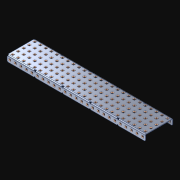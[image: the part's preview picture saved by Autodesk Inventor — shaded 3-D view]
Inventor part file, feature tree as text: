
AUTODESK INVENTOR PART (.ipt)
format: ipt  version: 2021 (Build 250183000, 183)  size: 2,157,568 bytes
history: native  units: in
note: dims shown in document units (in); Inventor stores cm internally (conversion verified against a paired STEP export)
features: extrude x176, other x176, sketch x4, pattern_linear x3
ambient origin geometry x8: Origin, YZ Plane, XZ Plane, XY Plane, X Axis, Y Axis, Z Axis, Center Point
bodies: Solid1 (feature_tree)
feature tree (359):
  pattern_linear  "Rectangular Pattern1"  Spacing1=0.182in  [1 undecoded]
  pattern_linear  "Rectangular Pattern2"  Spacing1=0.046in  [1 undecoded]
  pattern_linear  "Rectangular Pattern3"  Spacing1=0.5in  [1 undecoded]
  extrude  "Extrusion1"  Depth=9.8425in
  sketch  "Sketch1"  dims[d0=0.182in]
  other  "Srf1"
  sketch  "Sketch2"  dims[d1=0.046in d2=0.0in]
  other  "Srf2"
  sketch  "Sketch3"  dims[d3=0.182in]
  other  "Srf3"
  other  "Srf4"
  other  "Srf5"
  other  "Srf6"
  other  "Srf7"
  other  "Srf8"
  other  "Srf9"
  other  "Srf10"
  other  "Srf11"
  other  "Srf12"
  other  "Srf13"
  other  "Srf14"
  other  "Srf15"
  other  "Srf16"
  other  "Srf17"
  other  "Srf18"
  other  "Srf19"
  other  "Srf20"
  other  "Srf21"
  other  "Srf22"
  other  "Srf23"
  other  "Srf24"
  other  "Srf25"
  other  "Srf26"
  other  "Srf27"
  other  "Srf38"
  other  "Srf39"
  other  "Srf40"
  other  "Srf41"
  other  "Srf42"
  other  "Srf43"
  other  "Srf44"
  other  "Srf45"
  other  "Srf46"
  other  "Srf47"
  other  "Srf48"
  other  "Srf49"
  other  "Srf50"
  other  "Srf51"
  other  "Srf52"
  other  "Srf53"
  other  "Srf54"
  other  "Srf55"
  other  "Srf56"
  other  "Srf57"
  other  "Srf58"
  other  "Srf59"
  other  "Srf60"
  other  "Srf61"
  other  "Srf72"
  other  "Srf73"
  other  "Srf74"
  other  "Srf75"
  other  "Srf76"
  other  "Srf77"
  other  "Srf78"
  other  "Srf79"
  other  "Srf80"
  other  "Srf81"
  other  "Srf82"
  other  "Srf83"
  other  "Srf84"
  other  "Srf85"
  other  "Srf86"
  other  "Srf87"
  other  "Srf88"
  other  "Srf89"
  other  "Srf90"
  other  "Srf91"
  other  "Srf92"
  other  "Srf93"
  other  "Srf94"
  other  "Srf95"
  other  "Srf96"
  other  "Srf107"
  other  "Srf108"
  other  "Srf109"
  other  "Srf110"
  other  "Srf111"
  other  "Srf112"
  other  "Srf113"
  other  "Srf114"
  other  "Srf115"
  other  "Srf116"
  other  "Srf117"
  other  "Srf118"
  other  "Srf119"
  other  "Srf120"
  other  "Srf121"
  other  "Srf122"
  other  "Srf123"
  other  "Srf124"
  other  "Srf125"
  other  "Srf126"
  other  "Srf127"
  other  "Srf128"
  other  "Srf129"
  other  "Srf130"
  other  "Srf131"
  other  "Srf142"
  other  "Srf143"
  other  "Srf144"
  other  "Srf145"
  other  "Srf146"
  other  "Srf147"
  other  "Srf148"
  other  "Srf149"
  other  "Srf150"
  other  "Srf151"
  other  "Srf152"
  other  "Srf153"
  other  "Srf154"
  other  "Srf155"
  other  "Srf156"
  other  "Srf157"
  other  "Srf158"
  other  "Srf159"
  other  "Srf160"
  other  "Srf161"
  other  "Srf162"
  other  "Srf163"
  other  "Srf164"
  other  "Srf165"
  other  "Srf166"
  other  "Srf177"
  other  "Srf178"
  other  "Srf179"
  other  "Srf180"
  other  "Srf181"
  other  "Srf182"
  other  "Srf183"
  other  "Srf184"
  other  "Srf185"
  other  "Srf186"
  other  "Srf187"
  other  "Srf188"
  other  "Srf189"
  other  "Srf190"
  other  "Srf191"
  other  "Srf192"
  other  "Srf193"
  other  "Srf194"
  other  "Srf195"
  other  "Srf196"
  other  "Srf197"
  other  "Srf198"
  other  "Srf199"
  other  "Srf200"
  other  "Srf201"
  other  "Srf212"
  other  "Srf213"
  other  "Srf214"
  other  "Srf215"
  other  "Srf216"
  other  "Srf217"
  other  "Srf218"
  other  "Srf219"
  other  "Srf220"
  other  "Srf221"
  other  "Srf222"
  other  "Srf223"
  other  "Srf224"
  other  "Srf225"
  other  "Srf226"
  other  "Srf227"
  other  "Srf228"
  other  "Srf229"
  other  "Srf230"
  other  "Srf231"
  other  "Srf232"
  other  "Srf233"
  other  "Srf234"
  other  "Srf235"
  sketch  "Sketch4"  dims[d4=0.046in d5=0.0in d6=0.182in d7=0.046in d8=0.0in d11=0.5in d12=9.8425in d14=0.5in d15=1.9685in d17=0.5in d18=9.8425in d20=0.5in d21=5.0in d22=0.0in]
  parser-record x1  (decoder bookkeeping rows leaked as tree rows — omitted from the tree; the rows remain in map.json)
  extrude  "ExtrusionSrf1"  Depth=9.8425in
  extrude  "ExtrusionSrf2"  Depth=9.8425in
  extrude  "ExtrusionSrf3"  Depth=9.8425in
  extrude  "ExtrusionSrf4"  Depth=9.8425in
  extrude  "ExtrusionSrf5"  Depth=9.8425in
  extrude  "ExtrusionSrf6"  TaperAngle=0.0deg  [1 undecoded]
  extrude  "ExtrusionSrf7"  [1 undecoded]
  extrude  "ExtrusionSrf8"  [1 undecoded]
  extrude  "ExtrusionSrf9"  [1 undecoded]
  extrude  "ExtrusionSrf10"  [1 undecoded]
  extrude  "ExtrusionSrf11"  [1 undecoded]
  extrude  "ExtrusionSrf12"  [1 undecoded]
  extrude  "ExtrusionSrf13"  [1 undecoded]
  extrude  "ExtrusionSrf14"  [1 undecoded]
  extrude  "ExtrusionSrf15"  [1 undecoded]
  extrude  "ExtrusionSrf16"  [1 undecoded]
  extrude  "ExtrusionSrf17"  [1 undecoded]
  extrude  "ExtrusionSrf18"  [1 undecoded]
  extrude  "ExtrusionSrf19"  [1 undecoded]
  extrude  "ExtrusionSrf20"  [1 undecoded]
  extrude  "ExtrusionSrf21"  [1 undecoded]
  extrude  "ExtrusionSrf22"  [1 undecoded]
  extrude  "ExtrusionSrf23"  [1 undecoded]
  extrude  "ExtrusionSrf24"  [1 undecoded]
  extrude  "ExtrusionSrf25"  [1 undecoded]
  extrude  "ExtrusionSrf26"  [1 undecoded]
  extrude  "ExtrusionSrf27"  [1 undecoded]
  extrude  "ExtrusionSrf38"  [1 undecoded]
  extrude  "ExtrusionSrf39"  [1 undecoded]
  extrude  "ExtrusionSrf40"  [1 undecoded]
  extrude  "ExtrusionSrf41"  [1 undecoded]
  extrude  "ExtrusionSrf42"  [1 undecoded]
  extrude  "ExtrusionSrf43"  [1 undecoded]
  extrude  "ExtrusionSrf44"  [1 undecoded]
  extrude  "ExtrusionSrf45"  [1 undecoded]
  extrude  "ExtrusionSrf46"  [1 undecoded]
  extrude  "ExtrusionSrf47"  [1 undecoded]
  extrude  "ExtrusionSrf48"  [1 undecoded]
  extrude  "ExtrusionSrf49"  [1 undecoded]
  extrude  "ExtrusionSrf50"  [1 undecoded]
  extrude  "ExtrusionSrf51"  [1 undecoded]
  extrude  "ExtrusionSrf52"  [1 undecoded]
  extrude  "ExtrusionSrf53"  [1 undecoded]
  extrude  "ExtrusionSrf54"  [1 undecoded]
  extrude  "ExtrusionSrf55"  [1 undecoded]
  extrude  "ExtrusionSrf56"  [1 undecoded]
  extrude  "ExtrusionSrf57"  [1 undecoded]
  extrude  "ExtrusionSrf58"  [1 undecoded]
  extrude  "ExtrusionSrf59"  [1 undecoded]
  extrude  "ExtrusionSrf60"  [1 undecoded]
  extrude  "ExtrusionSrf61"  [1 undecoded]
  extrude  "ExtrusionSrf72"  [1 undecoded]
  extrude  "ExtrusionSrf73"  [1 undecoded]
  extrude  "ExtrusionSrf74"  [1 undecoded]
  extrude  "ExtrusionSrf75"  [1 undecoded]
  extrude  "ExtrusionSrf76"  [1 undecoded]
  extrude  "ExtrusionSrf77"  [1 undecoded]
  extrude  "ExtrusionSrf78"  [1 undecoded]
  extrude  "ExtrusionSrf79"  [1 undecoded]
  extrude  "ExtrusionSrf80"  [1 undecoded]
  extrude  "ExtrusionSrf81"  [1 undecoded]
  extrude  "ExtrusionSrf82"  [1 undecoded]
  extrude  "ExtrusionSrf83"  [1 undecoded]
  extrude  "ExtrusionSrf84"  [1 undecoded]
  extrude  "ExtrusionSrf85"  [1 undecoded]
  extrude  "ExtrusionSrf86"  [1 undecoded]
  extrude  "ExtrusionSrf87"  [1 undecoded]
  extrude  "ExtrusionSrf88"  [1 undecoded]
  extrude  "ExtrusionSrf89"  [1 undecoded]
  extrude  "ExtrusionSrf90"  [1 undecoded]
  extrude  "ExtrusionSrf91"  [1 undecoded]
  extrude  "ExtrusionSrf92"  [1 undecoded]
  extrude  "ExtrusionSrf93"  [1 undecoded]
  extrude  "ExtrusionSrf94"  [1 undecoded]
  extrude  "ExtrusionSrf95"  [1 undecoded]
  extrude  "ExtrusionSrf96"  [1 undecoded]
  extrude  "ExtrusionSrf107"  [1 undecoded]
  extrude  "ExtrusionSrf108"  [1 undecoded]
  extrude  "ExtrusionSrf109"  [1 undecoded]
  extrude  "ExtrusionSrf110"  [1 undecoded]
  extrude  "ExtrusionSrf111"  [1 undecoded]
  extrude  "ExtrusionSrf112"  [1 undecoded]
  extrude  "ExtrusionSrf113"  [1 undecoded]
  extrude  "ExtrusionSrf114"  [1 undecoded]
  extrude  "ExtrusionSrf115"  [1 undecoded]
  extrude  "ExtrusionSrf116"  [1 undecoded]
  extrude  "ExtrusionSrf117"  [1 undecoded]
  extrude  "ExtrusionSrf118"  [1 undecoded]
  extrude  "ExtrusionSrf119"  [1 undecoded]
  extrude  "ExtrusionSrf120"  [1 undecoded]
  extrude  "ExtrusionSrf121"  [1 undecoded]
  extrude  "ExtrusionSrf122"  [1 undecoded]
  extrude  "ExtrusionSrf123"  [1 undecoded]
  extrude  "ExtrusionSrf124"  [1 undecoded]
  extrude  "ExtrusionSrf125"  [1 undecoded]
  extrude  "ExtrusionSrf126"  [1 undecoded]
  extrude  "ExtrusionSrf127"  [1 undecoded]
  extrude  "ExtrusionSrf128"  [1 undecoded]
  extrude  "ExtrusionSrf129"  [1 undecoded]
  extrude  "ExtrusionSrf130"  [1 undecoded]
  extrude  "ExtrusionSrf131"  [1 undecoded]
  extrude  "ExtrusionSrf142"  [1 undecoded]
  extrude  "ExtrusionSrf143"  [1 undecoded]
  extrude  "ExtrusionSrf144"  [1 undecoded]
  extrude  "ExtrusionSrf145"  [1 undecoded]
  extrude  "ExtrusionSrf146"  [1 undecoded]
  extrude  "ExtrusionSrf147"  [1 undecoded]
  extrude  "ExtrusionSrf148"  [1 undecoded]
  extrude  "ExtrusionSrf149"  [1 undecoded]
  extrude  "ExtrusionSrf150"  [1 undecoded]
  extrude  "ExtrusionSrf151"  [1 undecoded]
  extrude  "ExtrusionSrf152"  [1 undecoded]
  extrude  "ExtrusionSrf153"  [1 undecoded]
  extrude  "ExtrusionSrf154"  [1 undecoded]
  extrude  "ExtrusionSrf155"  [1 undecoded]
  extrude  "ExtrusionSrf156"  [1 undecoded]
  extrude  "ExtrusionSrf157"  [1 undecoded]
  extrude  "ExtrusionSrf158"  [1 undecoded]
  extrude  "ExtrusionSrf159"  [1 undecoded]
  extrude  "ExtrusionSrf160"  [1 undecoded]
  extrude  "ExtrusionSrf161"  [1 undecoded]
  extrude  "ExtrusionSrf162"  [1 undecoded]
  extrude  "ExtrusionSrf163"  [1 undecoded]
  extrude  "ExtrusionSrf164"  [1 undecoded]
  extrude  "ExtrusionSrf165"  [1 undecoded]
  extrude  "ExtrusionSrf166"  [1 undecoded]
  extrude  "ExtrusionSrf177"  [1 undecoded]
  extrude  "ExtrusionSrf178"  [1 undecoded]
  extrude  "ExtrusionSrf179"  [1 undecoded]
  extrude  "ExtrusionSrf180"  [1 undecoded]
  extrude  "ExtrusionSrf181"  [1 undecoded]
  extrude  "ExtrusionSrf182"  [1 undecoded]
  extrude  "ExtrusionSrf183"  [1 undecoded]
  extrude  "ExtrusionSrf184"  [1 undecoded]
  extrude  "ExtrusionSrf185"  [1 undecoded]
  extrude  "ExtrusionSrf186"  [1 undecoded]
  extrude  "ExtrusionSrf187"  [1 undecoded]
  extrude  "ExtrusionSrf188"  [1 undecoded]
  extrude  "ExtrusionSrf189"  [1 undecoded]
  extrude  "ExtrusionSrf190"  [1 undecoded]
  extrude  "ExtrusionSrf191"  [1 undecoded]
  extrude  "ExtrusionSrf192"  [1 undecoded]
  extrude  "ExtrusionSrf193"  [1 undecoded]
  extrude  "ExtrusionSrf194"  [1 undecoded]
  extrude  "ExtrusionSrf195"  [1 undecoded]
  extrude  "ExtrusionSrf196"  [1 undecoded]
  extrude  "ExtrusionSrf197"  [1 undecoded]
  extrude  "ExtrusionSrf198"  [1 undecoded]
  extrude  "ExtrusionSrf199"  [1 undecoded]
  extrude  "ExtrusionSrf200"  [1 undecoded]
  extrude  "ExtrusionSrf201"  [1 undecoded]
  extrude  "ExtrusionSrf212"  [1 undecoded]
  extrude  "ExtrusionSrf213"  [1 undecoded]
  extrude  "ExtrusionSrf214"  [1 undecoded]
  extrude  "ExtrusionSrf215"  [1 undecoded]
  extrude  "ExtrusionSrf216"  [1 undecoded]
  extrude  "ExtrusionSrf217"  [1 undecoded]
  extrude  "ExtrusionSrf218"  [1 undecoded]
  extrude  "ExtrusionSrf219"  [1 undecoded]
  extrude  "ExtrusionSrf220"  [1 undecoded]
  extrude  "ExtrusionSrf221"  [1 undecoded]
  extrude  "ExtrusionSrf222"  [1 undecoded]
  extrude  "ExtrusionSrf223"  [1 undecoded]
  extrude  "ExtrusionSrf224"  [1 undecoded]
  extrude  "ExtrusionSrf225"  [1 undecoded]
  extrude  "ExtrusionSrf226"  [1 undecoded]
  extrude  "ExtrusionSrf227"  [1 undecoded]
  extrude  "ExtrusionSrf228"  [1 undecoded]
  extrude  "ExtrusionSrf229"  [1 undecoded]
  extrude  "ExtrusionSrf230"  [1 undecoded]
  extrude  "ExtrusionSrf231"  [1 undecoded]
  extrude  "ExtrusionSrf232"  [1 undecoded]
  extrude  "ExtrusionSrf233"  [1 undecoded]
  extrude  "ExtrusionSrf234"  [1 undecoded]
  extrude  "ExtrusionSrf235"  [1 undecoded]
note: 173 required parameter values undecoded (feature->parameter linkage not recoverable at this tier; creation-order binding heuristic only, values carry confidence <= 0.55)
